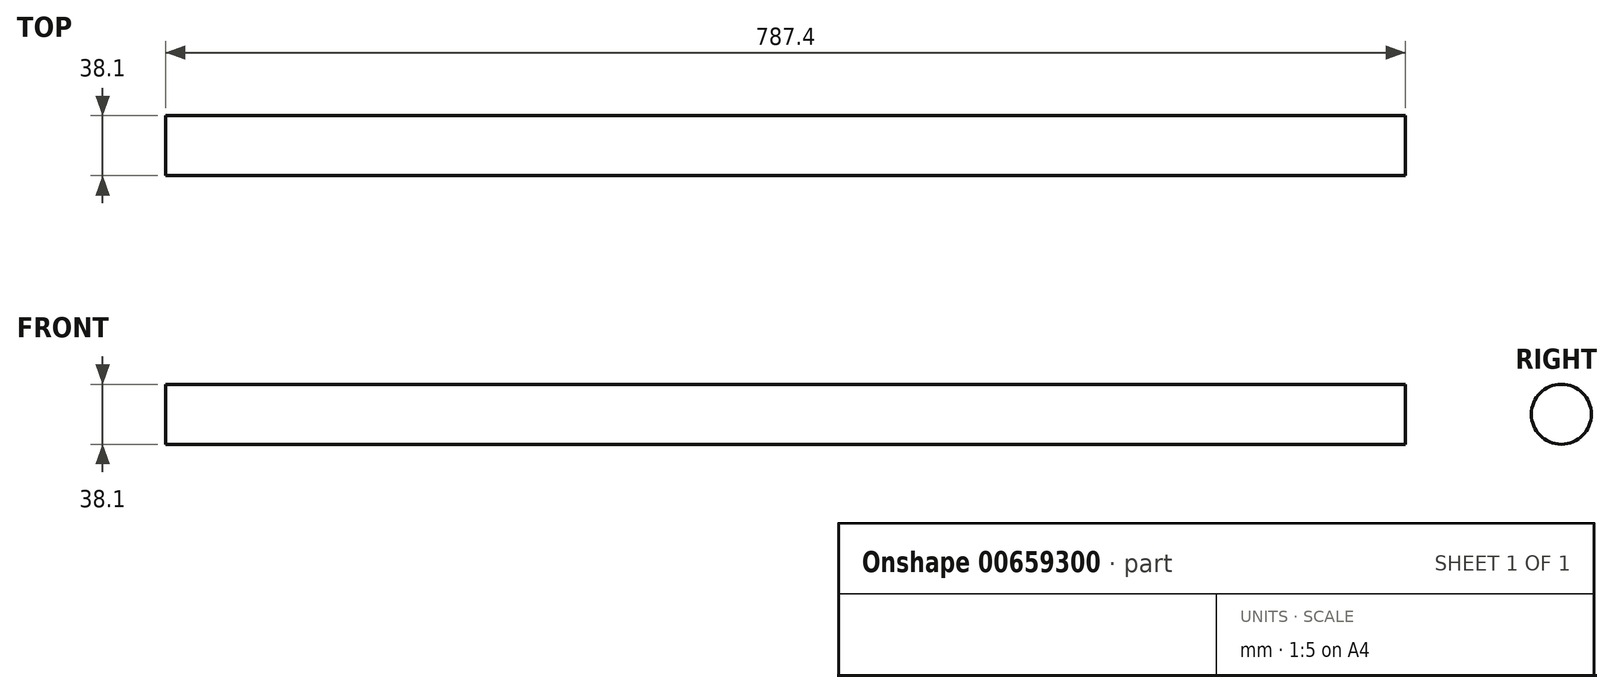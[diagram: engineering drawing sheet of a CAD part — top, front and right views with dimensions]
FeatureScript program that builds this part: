
annotation { "Feature Type Name" : "Feature", "Feature Type Description" : "" }
export const myFeature = defineFeature(function(context is Context, id is Id, definition is map)
    precondition{}
    {
        {
            var Q0;
            Q0=qCreatedBy(makeId("Right.planeOp"),FACE);
            var sketch = newSketch(context, id + "F0", { "sketchPlane" : qUnion([Q0])});
            skCircle(sketch, "E0", {"center": v(0, 0) * mm, "radius": 19.05 * mm});
            skSolve(sketch);
        }
        {
            var Q0;
            Q0=makeQuery(id+"F0.imprint","IMPRINT",FACE,{"disambiguationData":[TD([[makeQuery(id+"F0.imprint","IMPRINT",EDGE,{"derivedFrom":sQuery(id+"F0.wireOp",EDGE,"E0")}),1.0]])]});
            extrude(context, id + "F1", {"entities" : qUnion([Q0]), "depth" : 787.4 * mm, "offsetDistance" : 25.4 * mm});
        }
    });
